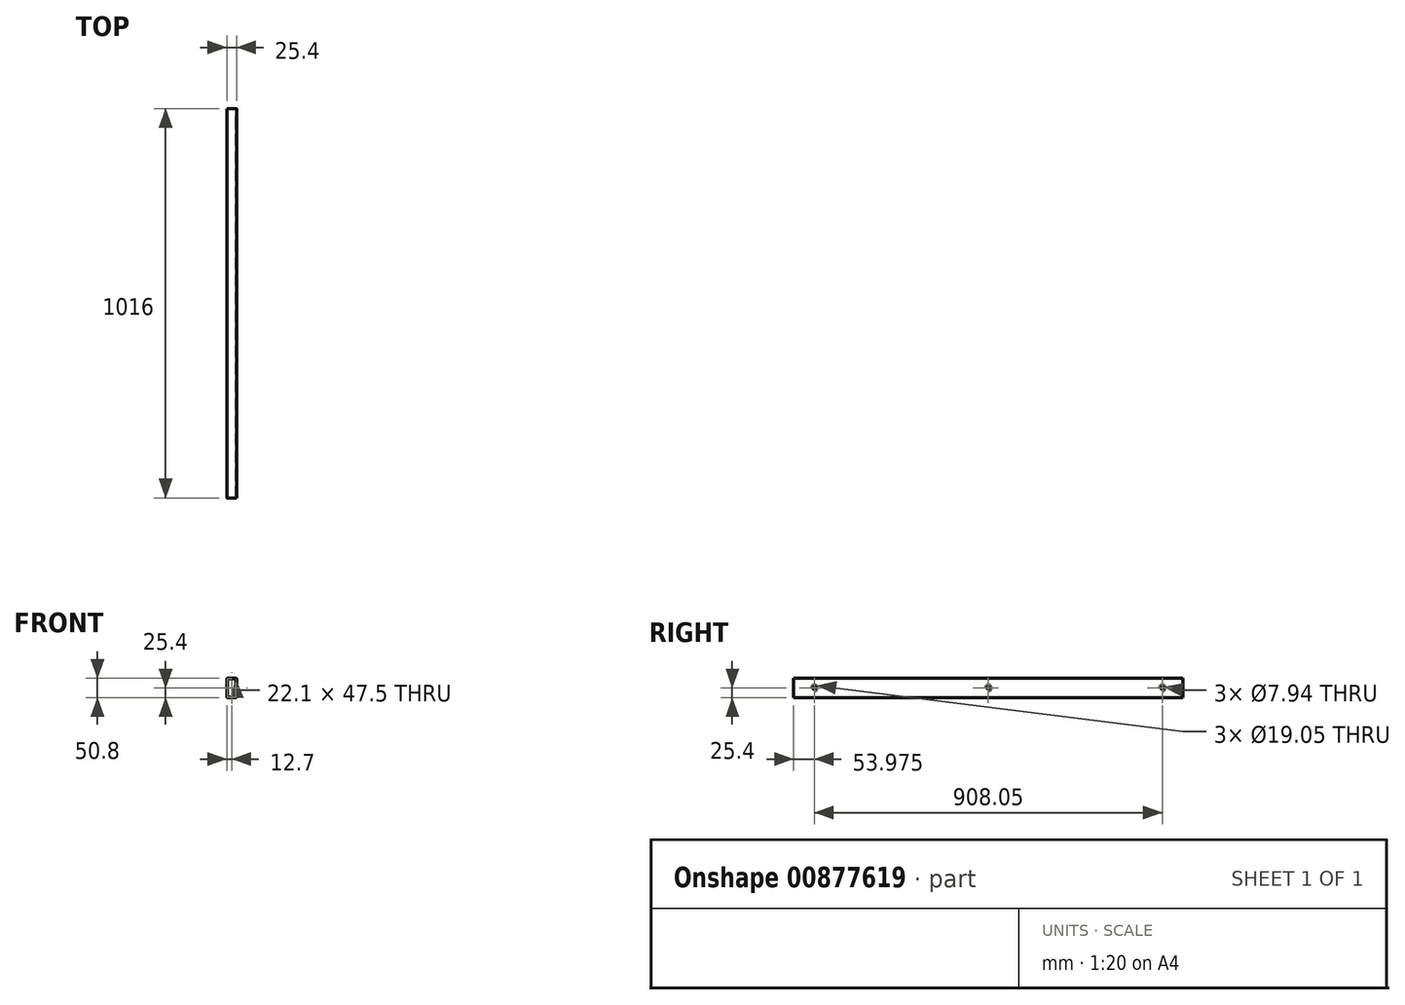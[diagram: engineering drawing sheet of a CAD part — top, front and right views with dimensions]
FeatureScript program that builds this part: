
annotation { "Feature Type Name" : "Feature", "Feature Type Description" : "" }
export const myFeature = defineFeature(function(context is Context, id is Id, definition is map)
    precondition{}
    {
        {
            var Q0;
            Q0=qCreatedBy(makeId("Front.planeOp"),FACE);
            var sketch = newSketch(context, id + "F0", { "sketchPlane" : qUnion([Q0])});
            skLineSegment(sketch, "E0.bottom", {"start": v(1.65, 0) * mm, "end": v(23.75, 0) * mm});
            skLineSegment(sketch, "E0.top", {"start": v(1.65, 50.8) * mm, "end": v(23.75, 50.8) * mm});
            skLineSegment(sketch, "E0.left", {"start": v(0, 1.65) * mm, "end": v(0, 49.15) * mm});
            skLineSegment(sketch, "E0.right", {"start": v(25.4, 1.65) * mm, "end": v(25.4, 49.15) * mm});
            skPoint(sketch, "E1.visualSharp", {"position": v(0, 50.8) * mm});
            skArc(sketch, "E1.filletArc", {"start": v(1.65, 50.8) * mm, "mid": v(0.48, 50.32) * mm, "end": v(0, 49.15) * mm});
            skPoint(sketch, "E2.visualSharp", {"position": v(25.4, 50.8) * mm});
            skArc(sketch, "E2.filletArc", {"start": v(25.4, 49.15) * mm, "mid": v(24.92, 50.32) * mm, "end": v(23.75, 50.8) * mm});
            skPoint(sketch, "E3.visualSharp", {"position": v(25.4, 0) * mm});
            skArc(sketch, "E3.filletArc", {"start": v(23.75, 0) * mm, "mid": v(24.92, 0.48) * mm, "end": v(25.4, 1.65) * mm});
            skPoint(sketch, "E4.visualSharp", {"position": v(0, 0) * mm});
            skArc(sketch, "E4.filletArc", {"start": v(0, 1.65) * mm, "mid": v(0.48, 0.48) * mm, "end": v(1.65, 0) * mm});
            skLineSegment(sketch, "E5.0", {"start": v(23.75, 1.65) * mm, "end": v(23.75, 49.15) * mm});
            skLineSegment(sketch, "E5.1", {"start": v(1.65, 1.65) * mm, "end": v(23.75, 1.65) * mm});
            skLineSegment(sketch, "E5.2", {"start": v(1.65, 1.65) * mm, "end": v(1.65, 49.15) * mm});
            skLineSegment(sketch, "E5.3", {"start": v(1.65, 49.15) * mm, "end": v(23.75, 49.15) * mm});
            skSolve(sketch);
        }
        {
            var Q0;
            Q0=qSketchRegion(id+"F0",true);
            extrude(context, id + "F1", {"entities" : qUnion([Q0]), "depth" : 1016 * mm, "offsetDistance" : 25.4 * mm});
        }
        {
            var Q0;
            Q0=makeQuery(id+"F1.opExtrude","SWEPT_FACE",FACE,{"disambiguationData":[OSD([sQuery(id+"F0.wireOp",EDGE,"E0.right")])]});
            var sketch = newSketch(context, id + "F2", { "sketchPlane" : qUnion([Q0])});
            skCircle(sketch, "E6", {"center": v(-508, 25.4) * mm, "radius": 3.97 * mm});
            skPoint(sketch, "E6.centerSnap0", {"position": v(-508, 49.15) * mm});
            skPoint(sketch, "E6.centerSnap1", {"position": v(0, 25.4) * mm});
            skCircle(sketch, "E7", {"center": v(-53.98, 25.4) * mm, "radius": 3.97 * mm});
            skCircle(sketch, "E8", {"center": v(-962.02, 25.4) * mm, "radius": 3.97 * mm});
            skPoint(sketch, "E8.centerSnap0", {"position": v(-1016, 25.4) * mm});
            skSolve(sketch);
        }
        {
            var Q0;
            Q0=qSketchRegion(id+"F2",true);
            extrude(context, id + "F3", {"entities" : qUnion([Q0]), "operationType" : NewBodyOperationType.REMOVE, "endBound" : BoundingType.UP_TO_NEXT, "oppositeDirection" : true, "depth" : 25.4 * mm, "offsetDistance" : 25.4 * mm});
        }
        {
            var Q0;
            Q0=makeQuery(id+"F1.opExtrude","SWEPT_FACE",FACE,{"disambiguationData":[OSD([sQuery(id+"F0.wireOp",EDGE,"E0.left")])]});
            var sketch = newSketch(context, id + "F4", { "sketchPlane" : qUnion([Q0])});
            skCircle(sketch, "E9", {"center": v(508, 25.4) * mm, "radius": 9.53 * mm});
            skPoint(sketch, "E9.centerSnap0", {"position": v(508, 49.15) * mm});
            skPoint(sketch, "E9.centerSnap1", {"position": v(0, 25.4) * mm});
            skCircle(sketch, "E10", {"center": v(53.98, 25.4) * mm, "radius": 9.53 * mm});
            skCircle(sketch, "E11", {"center": v(962.02, 25.4) * mm, "radius": 9.53 * mm});
            skPoint(sketch, "E11.centerSnap0", {"position": v(1016, 25.4) * mm});
            skSolve(sketch);
        }
        {
            var Q0;
            Q0=qSketchRegion(id+"F4",true);
            extrude(context, id + "F5", {"entities" : qUnion([Q0]), "operationType" : NewBodyOperationType.REMOVE, "endBound" : BoundingType.UP_TO_NEXT, "oppositeDirection" : true, "depth" : 25.4 * mm, "offsetDistance" : 25.4 * mm});
        }
    });
